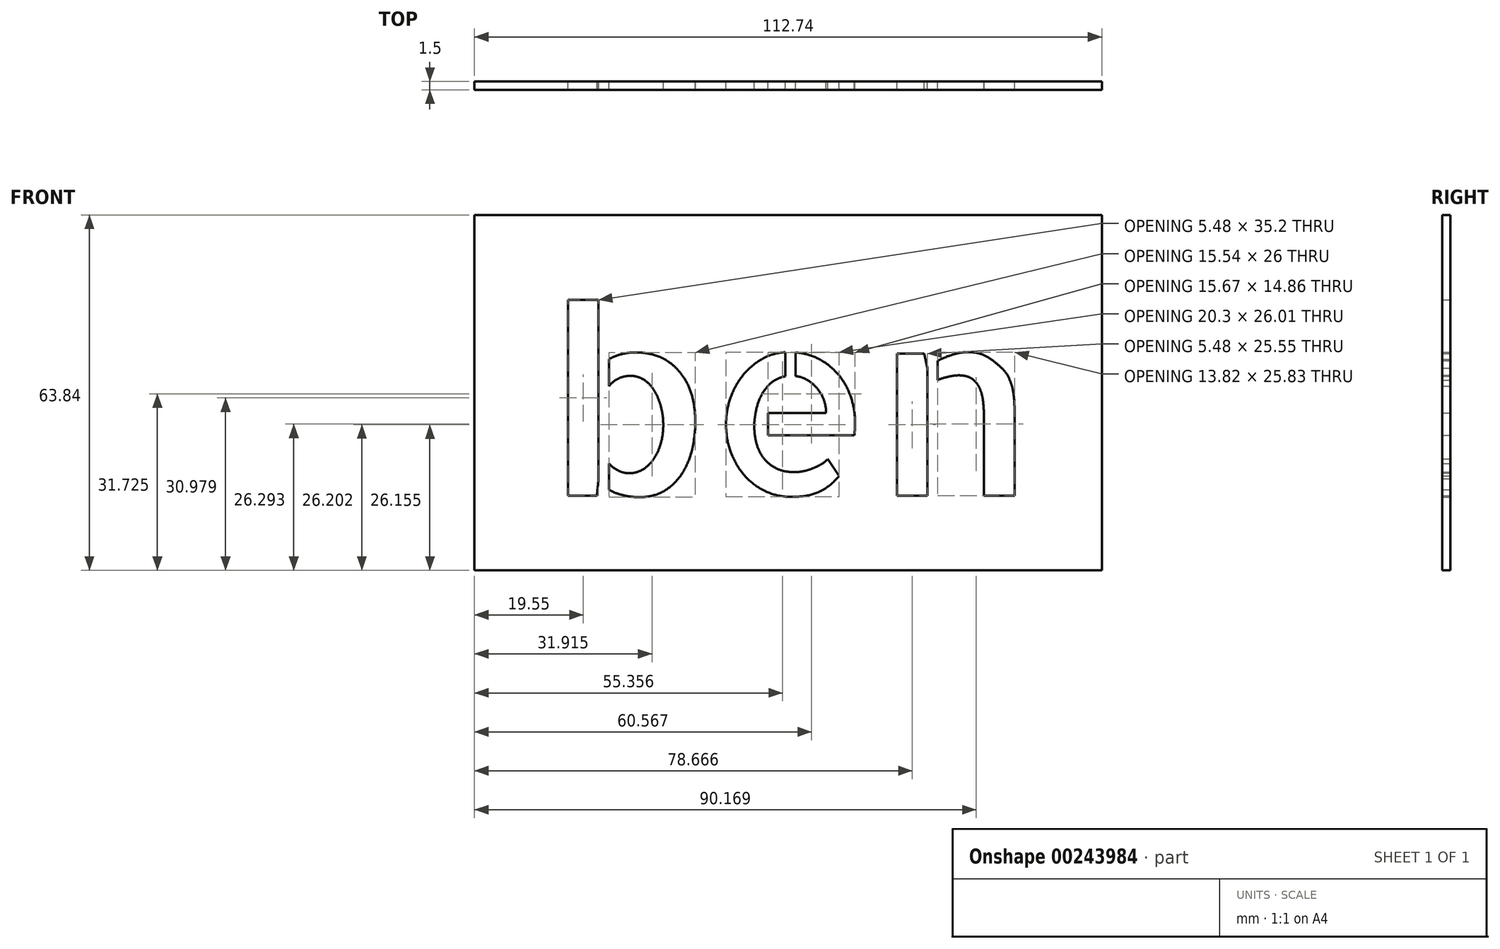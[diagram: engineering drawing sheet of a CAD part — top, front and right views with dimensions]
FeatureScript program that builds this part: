
annotation { "Feature Type Name" : "Feature", "Feature Type Description" : "" }
export const myFeature = defineFeature(function(context is Context, id is Id, definition is map)
    precondition{}
    {
        {
            var Q0;
            Q0=qCreatedBy(makeId("Front.planeOp"),FACE);
            var sketch = newSketch(context, id + "F0", { "sketchPlane" : qUnion([Q0])});
            skLineSegment(sketch, "E0.bottom", {"start": v(-56.37, 31.92) * mm, "end": v(56.37, 31.92) * mm});
            skLineSegment(sketch, "E0.top", {"start": v(-56.37, -31.92) * mm, "end": v(56.37, -31.92) * mm});
            skLineSegment(sketch, "E0.left", {"start": v(-56.37, 31.92) * mm, "end": v(-56.37, -31.92) * mm});
            skLineSegment(sketch, "E0.right", {"start": v(56.37, 31.92) * mm, "end": v(56.37, -31.92) * mm});
            skPoint(sketch, "E0.middle", {"position": v(0, 0) * mm});
            skText(sketch, "E1", { "text": "ben", "fontName": "AllertaStencil-Regular.ttf"});
            const initialGuessF0  = {"E1": [-0.04346, -0.01854, 1, 0, 0.0334]};
            skSetInitialGuess(sketch, initialGuessF0);
            skSolve(sketch);
        }
        {
            var Q0;
            Q0=makeQuery(id+"F0.imprint","IMPRINT",FACE,{"disambiguationData":[TD([[makeQuery(id+"F0.imprint","IMPRINT",EDGE,{"derivedFrom":sQuery(id+"F0.wireOp",EDGE,"E0.bottom")}),-1.0]])]});
            extrude(context, id + "F1", {"entities" : qUnion([Q0]), "depth" : 1.5 * mm});
        }
    });
